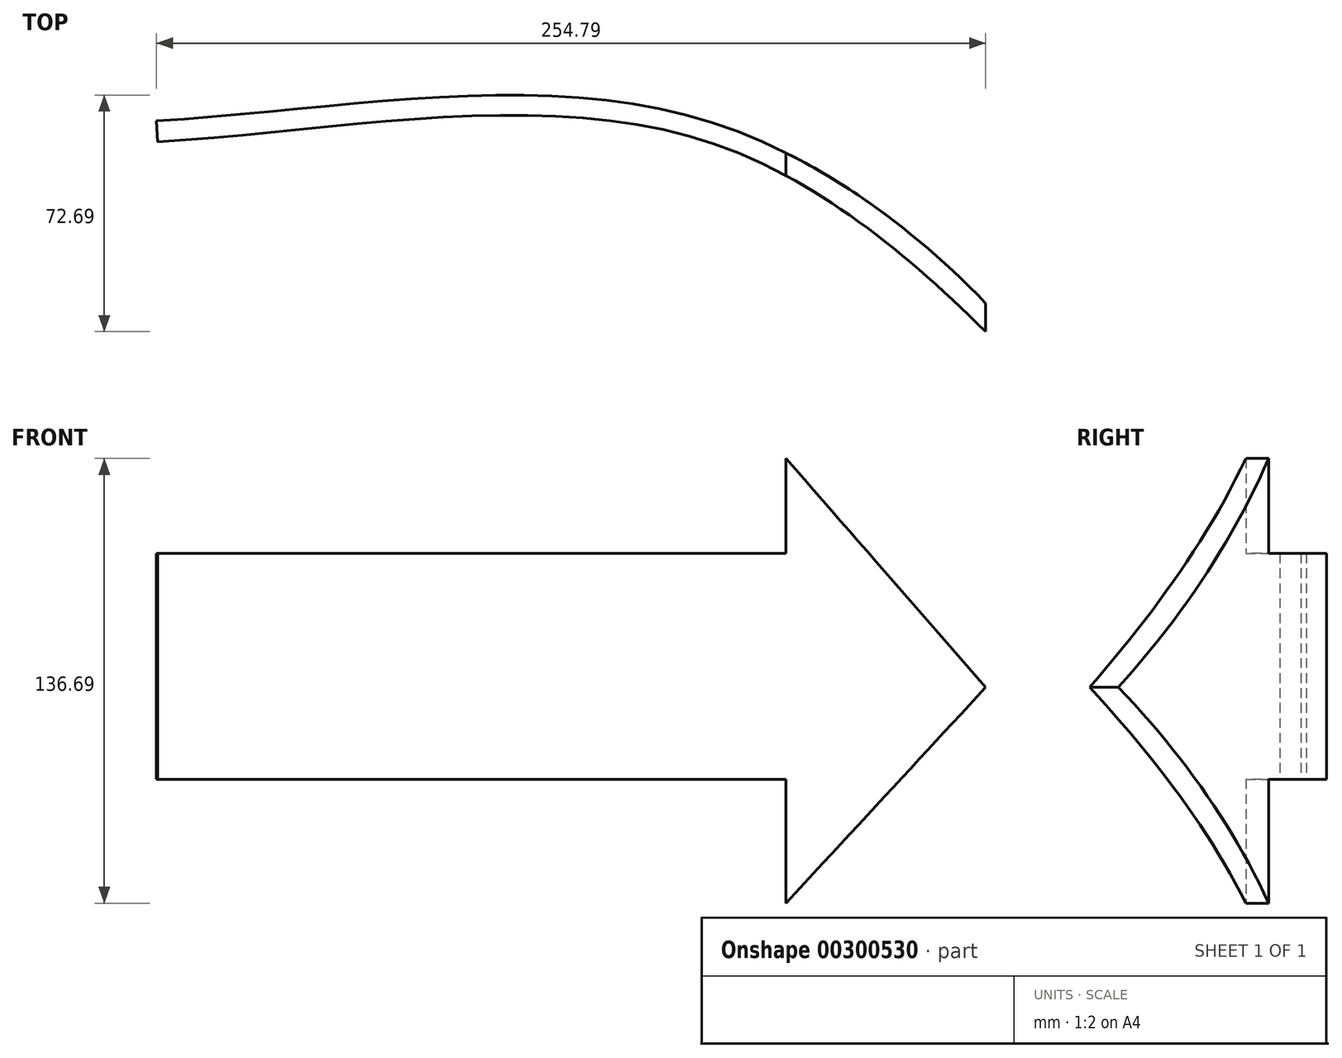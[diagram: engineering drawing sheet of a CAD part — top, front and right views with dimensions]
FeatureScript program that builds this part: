
annotation { "Feature Type Name" : "Feature", "Feature Type Description" : "" }
export const myFeature = defineFeature(function(context is Context, id is Id, definition is map)
    precondition{}
    {
        {
            var Q0;
            Q0=qCreatedBy(makeId("Top.planeOp"),FACE);
            var sketch = newSketch(context, id + "F0", { "sketchPlane" : qUnion([Q0])});
            skFitSpline(sketch, "E0", {"points": [v(-122.57, -6.48) * mm, v(47.78, -6.88) * mm, v(148.9, -82.02) * mm], "startDerivative": vector(317.64, 18.71) * mm, "endDerivative": vector(143.9, -146.78) * mm});
            skFitSpline(sketch, "E1", {"points": [v(-122.88, 0) * mm, v(48.44, -0.72) * mm, v(148.9, -76.34) * mm], "startDerivative": vector(317.48, 18.35) * mm, "endDerivative": vector(112.98, -157.3) * mm});
            skLineSegment(sketch, "E2", {"start": v(148.9, -82.02) * mm, "end": v(148.9, -76.34) * mm});
            skLineSegment(sketch, "E3", {"start": v(-122.57, -6.48) * mm, "end": v(-122.88, 0) * mm});
            skSolve(sketch);
        }
        {
            var Q0;
            Q0=qSketchRegion(id+"F0",true);
            extrude(context, id + "F1", {"entities" : qUnion([Q0]), "depth" : 152.4 * mm});
        }
        {
            var Q0;
            Q0=qCreatedBy(makeId("Front.planeOp"),FACE);
            var sketch = newSketch(context, id + "F2", { "sketchPlane" : qUnion([Q0])});
            skLineSegment(sketch, "E4.bottom", {"start": v(-132.65, 187.97) * mm, "end": v(70.55, 187.97) * mm});
            skLineSegment(sketch, "E4.top", {"start": v(-132.65, 111.77) * mm, "end": v(70.55, 111.77) * mm});
            skLineSegment(sketch, "E4.left", {"start": v(-132.65, 187.97) * mm, "end": v(-132.65, 111.77) * mm});
            skLineSegment(sketch, "E4.right", {"start": v(70.55, 187.97) * mm, "end": v(70.55, 111.77) * mm});
            skLineSegment(sketch, "E5.bottom", {"start": v(-132.65, 42.37) * mm, "end": v(70.55, 42.37) * mm});
            skLineSegment(sketch, "E5.top", {"start": v(-132.65, -33.83) * mm, "end": v(70.55, -33.83) * mm});
            skLineSegment(sketch, "E5.left", {"start": v(-132.65, 42.37) * mm, "end": v(-132.65, -33.83) * mm});
            skLineSegment(sketch, "E5.right", {"start": v(70.55, 42.37) * mm, "end": v(70.55, -33.83) * mm});
            skLineSegment(sketch, "E6", {"start": v(70.55, 4.27) * mm, "end": v(131.9, 70.64) * mm});
            skLineSegment(sketch, "E7", {"start": v(131.9, 70.64) * mm, "end": v(70.55, 140.96) * mm});
            skLineSegment(sketch, "E8", {"start": v(222.76, 167.83) * mm, "end": v(222.76, -50.38) * mm});
            skLineSegment(sketch, "E9", {"start": v(222.76, -50.38) * mm, "end": v(70.55, -50.38) * mm});
            skLineSegment(sketch, "E10", {"start": v(70.55, -50.38) * mm, "end": v(70.55, 4.27) * mm});
            skLineSegment(sketch, "E11", {"start": v(222.76, 167.83) * mm, "end": v(101.58, 191.28) * mm});
            skLineSegment(sketch, "E12", {"start": v(101.58, 191.28) * mm, "end": v(70.55, 171.98) * mm});
            skLineSegment(sketch, "E13", {"start": v(70.55, 171.98) * mm, "end": v(70.55, 140.96) * mm});
            skSolve(sketch);
        }
        {
            var Q0;
            Q0=qSketchRegion(id+"F2",true);
            extrude(context, id + "F3", {"entities" : qUnion([Q0]), "operationType" : NewBodyOperationType.REMOVE, "endBound" : BoundingType.THROUGH_ALL, "depth" : 25.4 * mm});
        }
        {
            var Q0;
            Q0=qSketchRegion(id+"F2",true);
            extrude(context, id + "F4", {"entities" : qUnion([Q0]), "operationType" : NewBodyOperationType.REMOVE, "endBound" : BoundingType.THROUGH_ALL, "oppositeDirection" : true, "depth" : 25.4 * mm});
        }
    });
